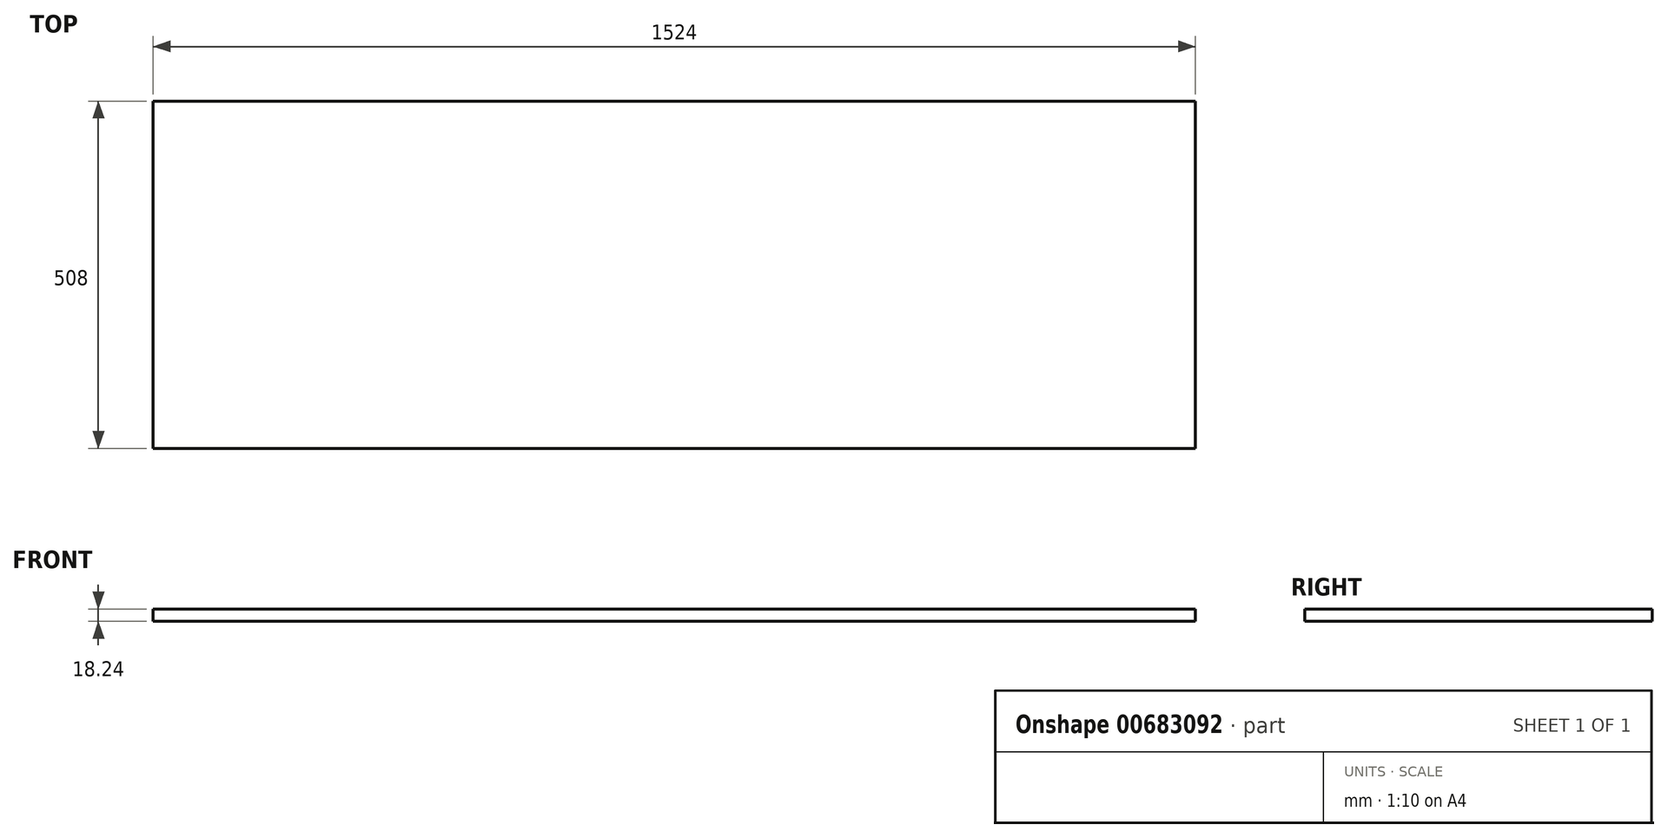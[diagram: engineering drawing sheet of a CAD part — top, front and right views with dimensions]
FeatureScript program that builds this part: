
annotation { "Feature Type Name" : "Feature", "Feature Type Description" : "" }
export const myFeature = defineFeature(function(context is Context, id is Id, definition is map)
    precondition{}
    {
        {
            var Q0;
            Q0=qCreatedBy(makeId("Top.planeOp"),FACE);
            var sketch = newSketch(context, id + "F0", { "sketchPlane" : qUnion([Q0])});
            skLineSegment(sketch, "E0.bottom", {"start": v(762, 254) * mm, "end": v(-762, 254) * mm});
            skLineSegment(sketch, "E0.top", {"start": v(762, -254) * mm, "end": v(-762, -254) * mm});
            skLineSegment(sketch, "E0.left", {"start": v(762, 254) * mm, "end": v(762, -254) * mm});
            skLineSegment(sketch, "E0.right", {"start": v(-762, 254) * mm, "end": v(-762, -254) * mm});
            skPoint(sketch, "E0.middle", {"position": v(0, 0) * mm});
            skSolve(sketch);
        }
        {
            var Q0;
            Q0 = qSketchRegion(id + "F0", true);
            extrude(context, id + "F1", {"entities" : qUnion([Q0]), "depth" : 18.24 * mm, "offsetDistance" : 25.4 * mm});
        }
    });
